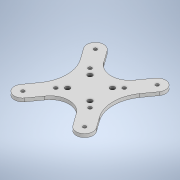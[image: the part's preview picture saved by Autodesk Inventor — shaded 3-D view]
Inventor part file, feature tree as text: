
AUTODESK INVENTOR PART (.ipt)
format: ipt  version: 2020 (Build 240168000, 168)  size: 194,048 bytes
history: native  units: mm
features: extrude x2, sketch x2
ambient origin geometry x8: Origin, YZ Plane, XZ Plane, XY Plane, X Axis, Y Axis, Z Axis, Center Point
bodies: Solid1 (feature_tree)
feature tree (4):
  extrude  "Extrusion1"  Depth=3.0mm
  extrude  "Extrusion2"  Depth=3.1mm
  sketch  "Sketch1"  dims[d0=3.0mm d1=0.0mm d2=3.1mm]
  sketch  "Sketch2"  dims[d3=3.1mm d4=3.1mm d5=3.1mm d6=0.0mm d7=0.0mm]
